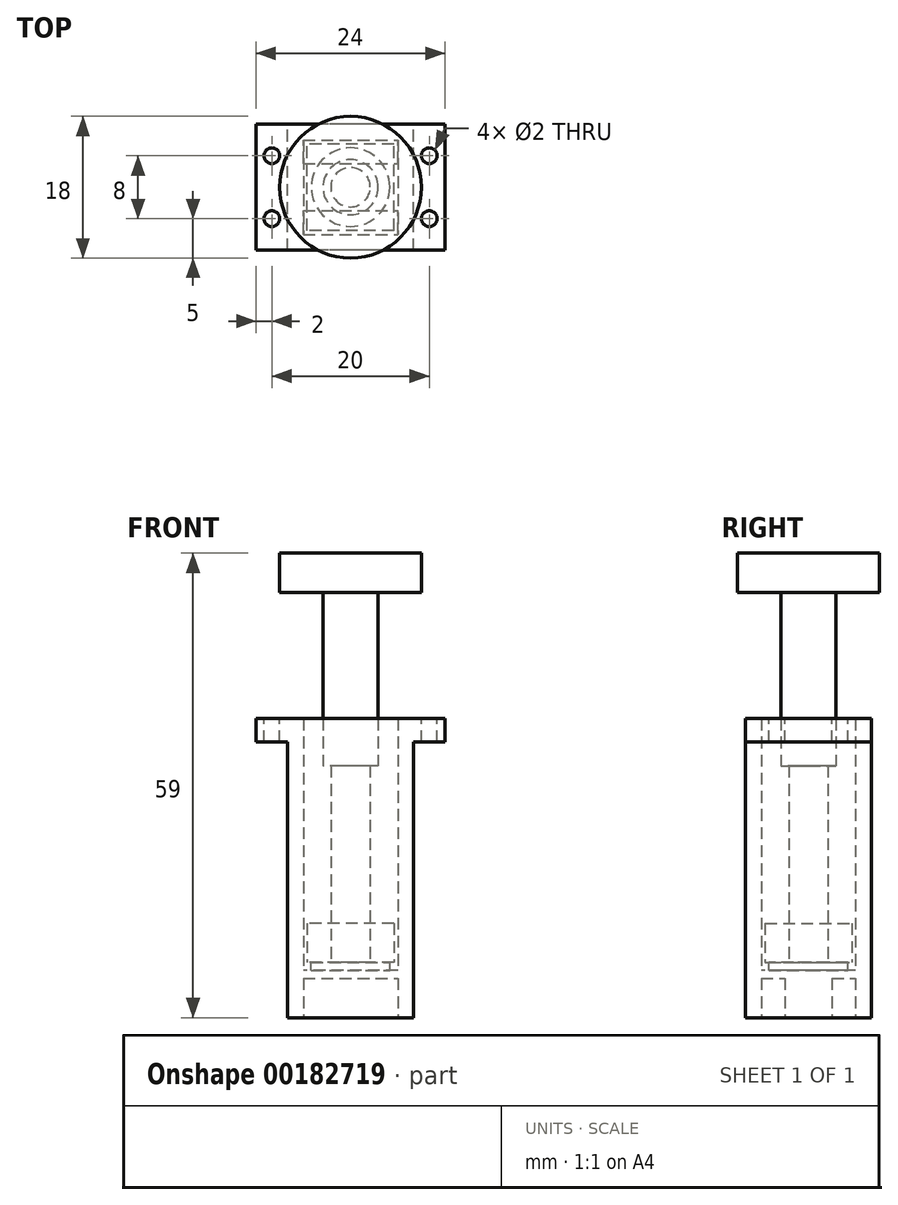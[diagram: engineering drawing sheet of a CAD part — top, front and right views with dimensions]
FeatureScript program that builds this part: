
annotation { "Feature Type Name" : "Feature", "Feature Type Description" : "" }
export const myFeature = defineFeature(function(context is Context, id is Id, definition is map)
    precondition{}
    {
        {
            var Q0;
            Q0=qCreatedBy(makeId("Top.planeOp"),FACE);
            var sketch = newSketch(context, id + "F0", { "sketchPlane" : qUnion([Q0])});
            skCircle(sketch, "E0", {"center": v(0, 0) * mm, "radius": 2.5 * mm});
            skSolve(sketch);
        }
        {
            var Q0;
            Q0 = qSketchRegion(id + "F0", true);
            extrude(context, id + "F1", {"entities" : qUnion([Q0]), "depth" : 23 * mm, "hasSecondDirection" : true, "secondDirectionOppositeDirection" : true, "secondDirectionDepth" : 25 * mm});
        }
        {
            var Q0;
            Q0=makeQuery(id+"F1.opExtrude","CAP_FACE",FACE,{"disambiguationData":[OSD([sQuery(id+"F0.wireOp",EDGE,"E0")])],"isStart":false});
            var sketch = newSketch(context, id + "F2", { "sketchPlane" : qUnion([Q0])});
            skCircle(sketch, "E1", {"center": v(0, 0) * mm, "radius": 6 * mm});
            skSolve(sketch);
        }
        {
            var Q0;
            Q0 = qSketchRegion(id + "F2", true);
            extrude(context, id + "F3", {"entities" : qUnion([Q0]), "operationType" : NewBodyOperationType.ADD, "depth" : 3 * mm});
        }
        {
            var Q0;
            Q0=qCreatedBy(makeId("Top.planeOp"),FACE);
            var sketch = newSketch(context, id + "F4", { "sketchPlane" : qUnion([Q0])});
            skCircle(sketch, "E2", {"center": v(0, 0) * mm, "radius": 3.5 * mm});
            skSolve(sketch);
        }
        {
            var Q0;
            Q0 = qSketchRegion(id + "F4", true);
            extrude(context, id + "F5", {"entities" : qUnion([Q0]), "depth" : 22 * mm});
        }
        {
            var Q0;
            Q0=makeQuery(id+"F5.opExtrude","CAP_FACE",FACE,{"disambiguationData":[OSD([sQuery(id+"F4.wireOp",EDGE,"E2")])],"isStart":false});
            var sketch = newSketch(context, id + "F6", { "sketchPlane" : qUnion([Q0])});
            skCircle(sketch, "E3", {"center": v(0, 0) * mm, "radius": 9 * mm});
            skSolve(sketch);
        }
        {
            var Q0;
            Q0 = qSketchRegion(id + "F6", true);
            extrude(context, id + "F7", {"entities" : qUnion([Q0]), "operationType" : NewBodyOperationType.ADD, "depth" : 5 * mm});
        }
        {
            var Q0;
            Q0=makeQuery(id+"F1.opExtrude","CAP_FACE",FACE,{"disambiguationData":[OSD([sQuery(id+"F0.wireOp",EDGE,"E0")])],"isStart":true});
            var sketch = newSketch(context, id + "F8", { "sketchPlane" : qUnion([Q0])});
            skLineSegment(sketch, "E4.bottom", {"start": v(5.5, 5.5) * mm, "end": v(-5.5, 5.5) * mm});
            skLineSegment(sketch, "E4.top", {"start": v(5.5, -5.5) * mm, "end": v(-5.5, -5.5) * mm});
            skLineSegment(sketch, "E4.left", {"start": v(5.5, 5.5) * mm, "end": v(5.5, -5.5) * mm});
            skLineSegment(sketch, "E4.right", {"start": v(-5.5, 5.5) * mm, "end": v(-5.5, -5.5) * mm});
            skPoint(sketch, "E4.middle", {"position": v(0, 0) * mm});
            skSolve(sketch);
        }
        {
            var Q0;
            Q0 = qSketchRegion(id + "F8", true);
            extrude(context, id + "F9", {"entities" : qUnion([Q0]), "oppositeDirection" : true, "depth" : 5 * mm});
        }
        {
            var Q0;
            Q0=makeQuery(id+"F9.opExtrude","CAP_FACE",FACE,{"disambiguationData":[OSD([sQuery(id+"F8.wireOp",EDGE,"E4.bottom"),sQuery(id+"F8.wireOp",EDGE,"E4.top"),sQuery(id+"F8.wireOp",EDGE,"E4.left"),sQuery(id+"F8.wireOp",EDGE,"E4.right")])],"isStart":true});
            var sketch = newSketch(context, id + "F10", { "sketchPlane" : qUnion([Q0])});
            skCircle(sketch, "E5", {"center": v(0, 0) * mm, "radius": 5 * mm});
            skSolve(sketch);
        }
        {
            var Q0;
            Q0 = qSketchRegion(id + "F10", true);
            extrude(context, id + "F11", {"entities" : qUnion([Q0]), "depth" : 1 * mm});
        }
        {
            var Q0;
            Q0=makeQuery(id+"F11.opExtrude","CAP_FACE",FACE,{"disambiguationData":[OSD([sQuery(id+"F10.wireOp",EDGE,"E5")])],"isStart":false});
            var sketch = newSketch(context, id + "F12", { "sketchPlane" : qUnion([Q0])});
            skLineSegment(sketch, "E6.bottom", {"start": v(6, -6) * mm, "end": v(-6, -6) * mm});
            skLineSegment(sketch, "E6.top", {"start": v(6, 6) * mm, "end": v(-6, 6) * mm});
            skLineSegment(sketch, "E6.left", {"start": v(6, -6) * mm, "end": v(6, 6) * mm});
            skLineSegment(sketch, "E6.right", {"start": v(-6, -6) * mm, "end": v(-6, 6) * mm});
            skPoint(sketch, "E6.middle", {"position": v(0, 0) * mm});
            skSolve(sketch);
        }
        {
            var Q0;
            Q0 = qSketchRegion(id + "F12", true);
            extrude(context, id + "F13", {"entities" : qUnion([Q0]), "operationType" : NewBodyOperationType.ADD, "depth" : 3 * mm});
        }
        {
            var Q0;
            Q0=makeQuery(id+"F13.opExtrude","CAP_FACE",FACE,{"disambiguationData":[OSD([sQuery(id+"F12.wireOp",EDGE,"E6.bottom"),sQuery(id+"F12.wireOp",EDGE,"E6.top"),sQuery(id+"F12.wireOp",EDGE,"E6.left"),sQuery(id+"F12.wireOp",EDGE,"E6.right")])],"isStart":false});
            var sketch = newSketch(context, id + "F14", { "sketchPlane" : qUnion([Q0])});
            skLineSegment(sketch, "E7.bottom", {"start": v(8, 8) * mm, "end": v(-8, 8) * mm});
            skLineSegment(sketch, "E7.top", {"start": v(8, -8) * mm, "end": v(-8, -8) * mm});
            skLineSegment(sketch, "E7.left", {"start": v(8, 8) * mm, "end": v(8, -8) * mm});
            skLineSegment(sketch, "E7.right", {"start": v(-8, 8) * mm, "end": v(-8, -8) * mm});
            skPoint(sketch, "E7.middle", {"position": v(0, 0) * mm});
            skLineSegment(sketch, "E8.bottom", {"start": v(6, 6) * mm, "end": v(-6, 6) * mm});
            skLineSegment(sketch, "E8.top", {"start": v(6, -6) * mm, "end": v(-6, -6) * mm});
            skLineSegment(sketch, "E8.left", {"start": v(6, 6) * mm, "end": v(6, -6) * mm});
            skLineSegment(sketch, "E8.right", {"start": v(-6, 6) * mm, "end": v(-6, -6) * mm});
            skSolve(sketch);
        }
        {
            var Q0;
            Q0 = qSketchRegion(id + "F14", true);
            extrude(context, id + "F15", {"entities" : qUnion([Q0]), "oppositeDirection" : true, "depth" : 35 * mm});
        }
        {
            var Q0;
            Q0=makeQuery(id+"F15.opExtrude","CAP_FACE",FACE,{"disambiguationData":[OSD([sQuery(id+"F14.wireOp",EDGE,"E7.bottom"),sQuery(id+"F14.wireOp",EDGE,"E7.top"),sQuery(id+"F14.wireOp",EDGE,"E7.left"),sQuery(id+"F14.wireOp",EDGE,"E7.right"),sQuery(id+"F14.wireOp",EDGE,"E8.bottom"),sQuery(id+"F14.wireOp",EDGE,"E8.top"),sQuery(id+"F14.wireOp",EDGE,"E8.left"),sQuery(id+"F14.wireOp",EDGE,"E8.right")])],"isStart":false});
            var sketch = newSketch(context, id + "F16", { "sketchPlane" : qUnion([Q0])});
            skLineSegment(sketch, "E9.bottom", {"start": v(-8, 8) * mm, "end": v(-12, 8) * mm});
            skLineSegment(sketch, "E9.top", {"start": v(-8, -8) * mm, "end": v(-12, -8) * mm});
            skLineSegment(sketch, "E9.left", {"start": v(-8, 8) * mm, "end": v(-8, -8) * mm});
            skLineSegment(sketch, "E9.right", {"start": v(-12, 8) * mm, "end": v(-12, -8) * mm});
            skLineSegment(sketch, "E10.bottom", {"start": v(8, 8) * mm, "end": v(12, 8) * mm});
            skLineSegment(sketch, "E10.top", {"start": v(8, -8) * mm, "end": v(12, -8) * mm});
            skLineSegment(sketch, "E10.left", {"start": v(8, 8) * mm, "end": v(8, -8) * mm});
            skLineSegment(sketch, "E10.right", {"start": v(12, 8) * mm, "end": v(12, -8) * mm});
            skCircle(sketch, "E11", {"center": v(-10, 4) * mm, "radius": 1 * mm});
            skCircle(sketch, "E12", {"center": v(-10, -4) * mm, "radius": 1 * mm});
            skCircle(sketch, "E13", {"center": v(10, 4) * mm, "radius": 1 * mm});
            skCircle(sketch, "E14", {"center": v(10, -4) * mm, "radius": 1 * mm});
            skSolve(sketch);
        }
        {
            var Q0;
            Q0 = qSketchRegion(id + "F16", true);
            extrude(context, id + "F17", {"entities" : qUnion([Q0]), "operationType" : NewBodyOperationType.ADD, "oppositeDirection" : true, "depth" : 3 * mm});
        }
        {
            var Q0;
            Q0=makeQuery(id+"F15.opExtrude","CAP_FACE",FACE,{"disambiguationData":[OSD([sQuery(id+"F14.wireOp",EDGE,"E7.bottom"),sQuery(id+"F14.wireOp",EDGE,"E7.top"),sQuery(id+"F14.wireOp",EDGE,"E7.left"),sQuery(id+"F14.wireOp",EDGE,"E7.right"),sQuery(id+"F14.wireOp",EDGE,"E8.bottom"),sQuery(id+"F14.wireOp",EDGE,"E8.top"),sQuery(id+"F14.wireOp",EDGE,"E8.left"),sQuery(id+"F14.wireOp",EDGE,"E8.right")])],"isStart":true});
            var sketch = newSketch(context, id + "F18", { "sketchPlane" : qUnion([Q0])});
            skLineSegment(sketch, "E15.bottom", {"start": v(-8, 8) * mm, "end": v(8, 8) * mm});
            skLineSegment(sketch, "E15.top", {"start": v(-8, -8) * mm, "end": v(8, -8) * mm});
            skLineSegment(sketch, "E15.left", {"start": v(-8, 8) * mm, "end": v(-8, -8) * mm});
            skLineSegment(sketch, "E15.right", {"start": v(8, 8) * mm, "end": v(8, -8) * mm});
            skPoint(sketch, "E15.middle", {"position": v(0, 0) * mm});
            skSolve(sketch);
        }
        {
            var Q0;
            Q0 = qSketchRegion(id + "F18", true);
            extrude(context, id + "F19", {"entities" : qUnion([Q0]), "operationType" : NewBodyOperationType.ADD, "depth" : 3 * mm});
        }
        {
            var Q0;
            Q0=makeQuery(id+"F19.opExtrude","CAP_FACE",FACE,{"disambiguationData":[OSD([sQuery(id+"F18.wireOp",EDGE,"E15.bottom"),sQuery(id+"F18.wireOp",EDGE,"E15.top"),sQuery(id+"F18.wireOp",EDGE,"E15.left"),sQuery(id+"F18.wireOp",EDGE,"E15.right")])],"isStart":false});
            var sketch = newSketch(context, id + "F20", { "sketchPlane" : qUnion([Q0])});
            skLineSegment(sketch, "E16.bottom", {"start": v(-6, 6) * mm, "end": v(6, 6) * mm});
            skLineSegment(sketch, "E16.top", {"start": v(-6, 3) * mm, "end": v(6, 3) * mm});
            skLineSegment(sketch, "E16.left", {"start": v(-6, 6) * mm, "end": v(-6, 3) * mm});
            skLineSegment(sketch, "E16.right", {"start": v(6, 6) * mm, "end": v(6, 3) * mm});
            skLineSegment(sketch, "E17.bottom", {"start": v(-6, -3) * mm, "end": v(6, -3) * mm});
            skLineSegment(sketch, "E17.top", {"start": v(-6, -6) * mm, "end": v(6, -6) * mm});
            skLineSegment(sketch, "E17.left", {"start": v(-6, -3) * mm, "end": v(-6, -6) * mm});
            skLineSegment(sketch, "E17.right", {"start": v(6, -3) * mm, "end": v(6, -6) * mm});
            skSolve(sketch);
        }
        {
            var Q0;
            Q0 = qSketchRegion(id + "F20", true);
            extrude(context, id + "F21", {"entities" : qUnion([Q0]), "operationType" : NewBodyOperationType.REMOVE, "oppositeDirection" : true, "depth" : 5 * mm});
        }
    });
